# Revit family: CSWEU2LED
name_source: partatom
category: Lighting Fixtures
revit_build: Autodesk Revit 2013 (Build: 20120221_2030(x64)
units: mm (PartAtom-declared; Revit-internal decimal feet)

## types (1)
- CSWEU2LED
    Apparent Load = 2 VA
    Default Elevation = 48 "
    Description = Outdoor LED emergency light with fully gasketed polycarbonate shield
    Glass Shield = Hubbell - White Glass
    Is 120V = No
    Is 270V = Yes
    Lamp = LED life-cycle of more than 10 years
    Load Classification = Lighting
    Manufacturer = Compass Lighting
    Manufacturer Fax = 864-678-1065
    Material = Hubbell-White
    Model = CSWEU2LED
    Mounting = Wall or Ceiling mount
    Photometric Link = http://www.compasslightingproducts.com
    Power Factor = 1
    Product Documentation Link = http://cdn.compasslightingproducts.com
    Product Page URL = http://www.compasslightingproducts.com
    URL = http://www.compasslightingproducts.com
    Voltage = 270 V
    Warranty = 2 year full unit warranty
    Watt = 2 W
    Wattage Comments = 1.15W per lamp

## geometry (parser evidence)
native form markers: Blend x22, Sweep x4
no freeform markers — native parametric forms only
